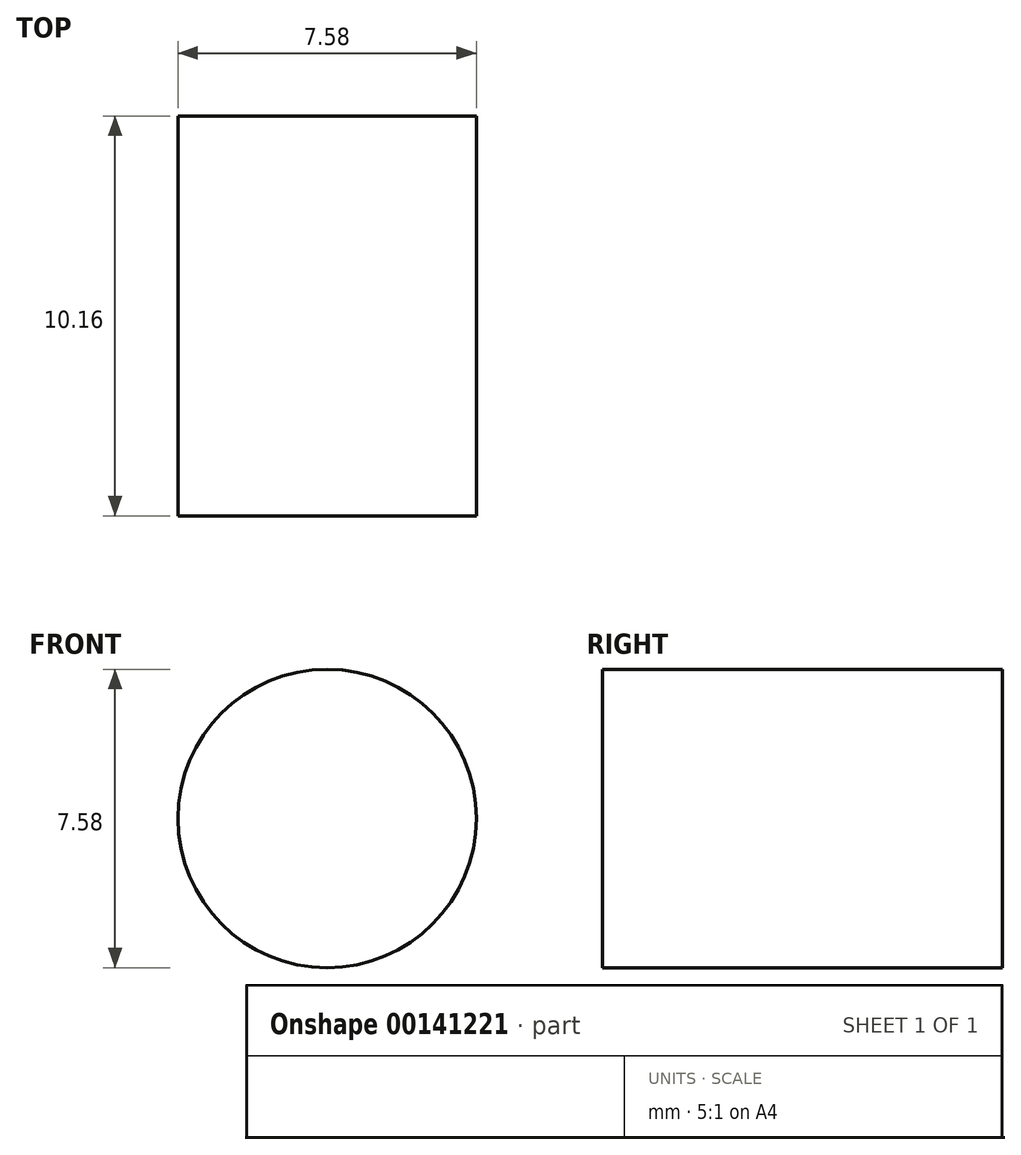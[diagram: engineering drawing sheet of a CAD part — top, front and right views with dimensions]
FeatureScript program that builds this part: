
annotation { "Feature Type Name" : "Feature", "Feature Type Description" : "" }
export const myFeature = defineFeature(function(context is Context, id is Id, definition is map)
    precondition{}
    {
        {
            var Q0;
            Q0=qCreatedBy(makeId("Front.planeOp"),FACE);
            var sketch = newSketch(context, id + "F0", { "sketchPlane" : qUnion([Q0])});
            skCircle(sketch, "E0", {"center": v(-26.56, 26.24) * mm, "radius": 3.8 * mm});
            skSolve(sketch);
        }
        {
            var Q0;
            Q0 = qSketchRegion(id + "F0", true);
            extrude(context, id + "F1", {"entities" : qUnion([Q0]), "depth" : 10.16 * mm});
        }
    });
